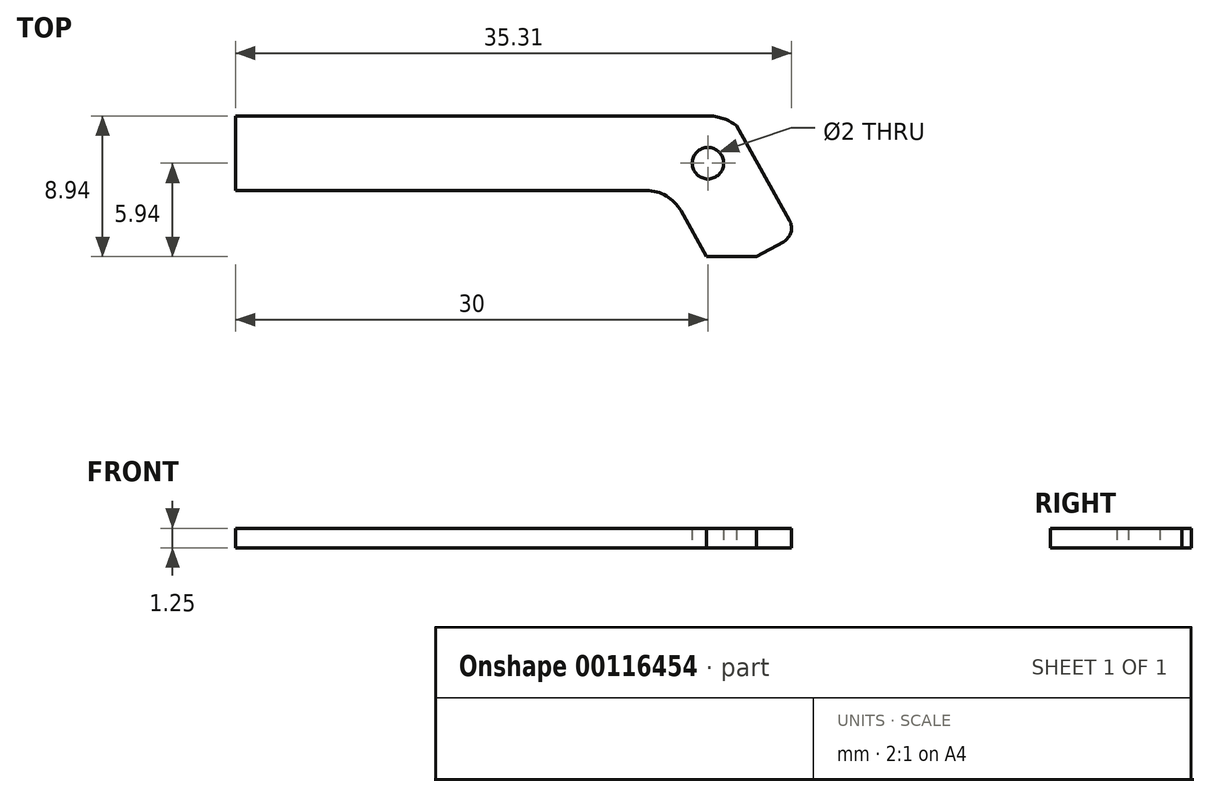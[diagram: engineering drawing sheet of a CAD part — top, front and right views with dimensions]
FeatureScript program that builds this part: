
annotation { "Feature Type Name" : "Feature", "Feature Type Description" : "" }
export const myFeature = defineFeature(function(context is Context, id is Id, definition is map)
    precondition{}
    {
        {
            var Q0;
            Q0=qCreatedBy(makeId("Top.planeOp"),FACE);
            var sketch = newSketch(context, id + "F0", { "sketchPlane" : qUnion([Q0])});
            skCircle(sketch, "E0", {"center": v(0, 0) * mm, "radius": 1 * mm});
            skArc(sketch, "E1", {"start": v(1.81, 2.4) * mm, "mid": v(0.95, 2.84) * mm, "end": v(0, 3) * mm});
            skLineSegment(sketch, "E2", {"start": v(-1.73, -3.02) * mm, "end": v(-0.1, -5.94) * mm});
            skLineSegment(sketch, "E3", {"start": v(1.81, 2.4) * mm, "end": v(5.18, -3.63) * mm});
            skLineSegment(sketch, "E4", {"start": v(3.1, -5.94) * mm, "end": v(-0.1, -5.94) * mm});
            skLineSegment(sketch, "E5", {"start": v(3.1, -5.94) * mm, "end": v(4.8, -5) * mm});
            skLineSegment(sketch, "E6", {"start": v(-3.9, -1.74) * mm, "end": v(-30, -1.74) * mm});
            skLineSegment(sketch, "E7", {"start": v(0, 3) * mm, "end": v(-30, 3) * mm});
            skLineSegment(sketch, "E8", {"start": v(-30, 3) * mm, "end": v(-30, -1.74) * mm});
            skPoint(sketch, "E9.visualSharp", {"position": v(-2.44, -1.74) * mm});
            skArc(sketch, "E9.filletArc", {"start": v(-1.73, -3.02) * mm, "mid": v(-2.64, -2.09) * mm, "end": v(-3.9, -1.74) * mm});
            skPoint(sketch, "E10.visualSharp", {"position": v(5.67, -4.5) * mm});
            skArc(sketch, "E10.filletArc", {"start": v(4.8, -5) * mm, "mid": v(5.27, -4.4) * mm, "end": v(5.18, -3.63) * mm});
            skSolve(sketch);
        }
        {
            var Q0;
            Q0=makeQuery(id+"F0.imprint","IMPRINT",FACE,{"disambiguationData":[TD([[makeQuery(id+"F0.imprint","IMPRINT",EDGE,{"derivedFrom":sQuery(id+"F0.wireOp",EDGE,"E0")}),-1.0]])]});
            extrude(context, id + "F1", {"entities" : qUnion([Q0]), "depth" : 1.25 * mm});
        }
    });
